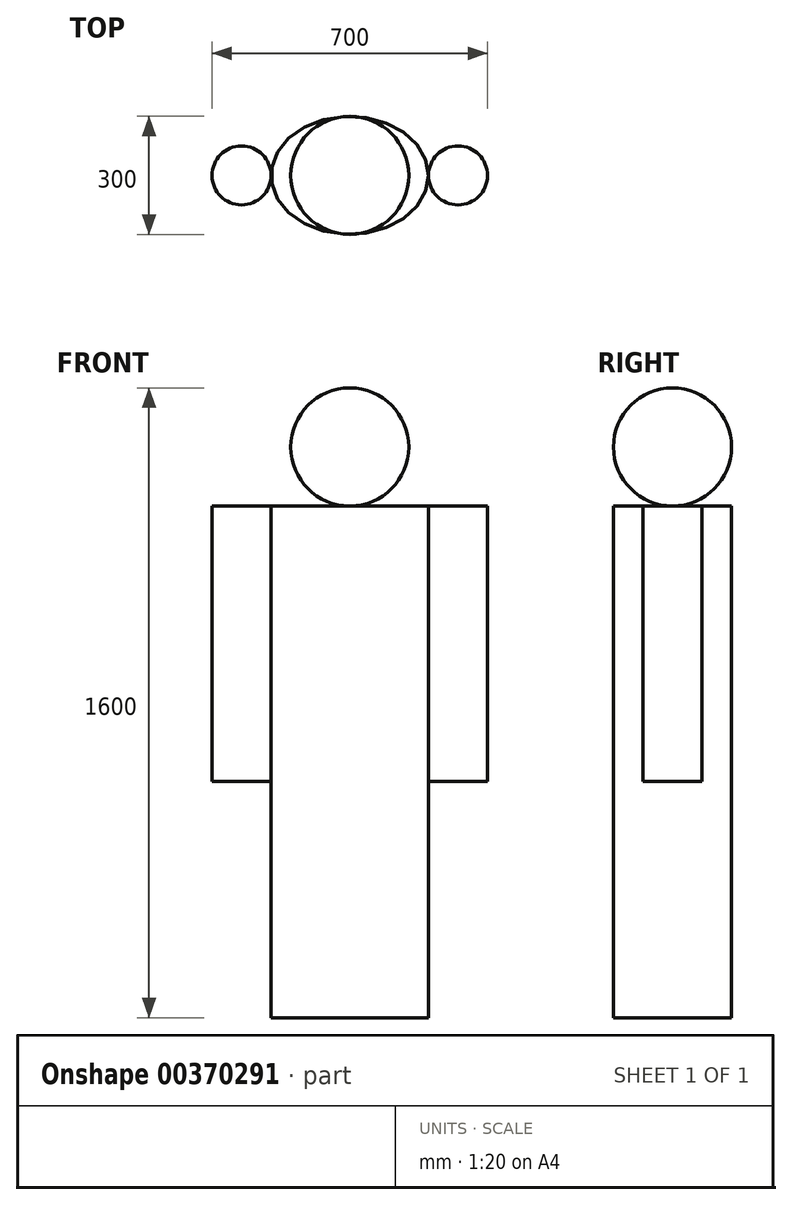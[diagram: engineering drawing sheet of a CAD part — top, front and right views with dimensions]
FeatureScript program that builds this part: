
annotation { "Feature Type Name" : "Feature", "Feature Type Description" : "" }
export const myFeature = defineFeature(function(context is Context, id is Id, definition is map)
    precondition{}
    {
        {
            var Q0;
            Q0=qCreatedBy(makeId("Top.planeOp"),FACE);
            var sketch = newSketch(context, id + "F0", { "sketchPlane" : qUnion([Q0])});
            skCircle(sketch, "E0", {"center": v(275, 0) * mm, "radius": 75 * mm});
            skCircle(sketch, "E1", {"center": v(-275, 0) * mm, "radius": 75 * mm});
            skEllipse(sketch, "E2", {"center": v(0, 0) * mm, "majorRadius": 200 * mm, "minorRadius": 150 * mm, "majorAxis": v(1, 0)});
            skSolve(sketch);
        }
        {
            var Q0;
            Q0=qCreatedBy(makeId("Front.planeOp"),FACE);
            var sketch = newSketch(context, id + "F1", { "sketchPlane" : qUnion([Q0])});
            skArc(sketch, "E3", {"start": v(0, 700) * mm, "mid": v(150, 850) * mm, "end": v(0, 1000) * mm});
            skLineSegment(sketch, "E4", {"start": v(0, 1000) * mm, "end": v(0, 700) * mm});
            skSolve(sketch);
        }
        {
            var Q0;
            Q0=makeQuery(id+"F1.imprint","IMPRINT",FACE,{"disambiguationData":[TD([[makeQuery(id+"F1.imprint","IMPRINT",EDGE,{"derivedFrom":sQuery(id+"F1.wireOp",EDGE,"E3")}),1.0]])]});
            var Q1;
            Q1=sQuery(id+"F1.wireOp",EDGE,"E4");
            revolve(context, id + "F2", {"entities" : qUnion([Q0]), "axis" : qUnion([Q1]), "revolveType" : RevolveType.FULL});
        }
        {
            var Q0;
            Q0=qSketchRegion(id+"F0",true);
            extrude(context, id + "F3", {"entities" : qUnion([Q0]), "depth" : 700 * mm});
        }
        {
            var Q0;
            Q0=makeQuery(id+"F3.opExtrude","CAP_FACE",FACE,{"disambiguationData":[OSD([sQuery(id+"F0.wireOp",EDGE,"E2")])],"isStart":true});
            extrude(context, id + "F4", {"entities" : qUnion([Q0]), "operationType" : NewBodyOperationType.ADD, "depth" : 600 * mm});
        }
    });
